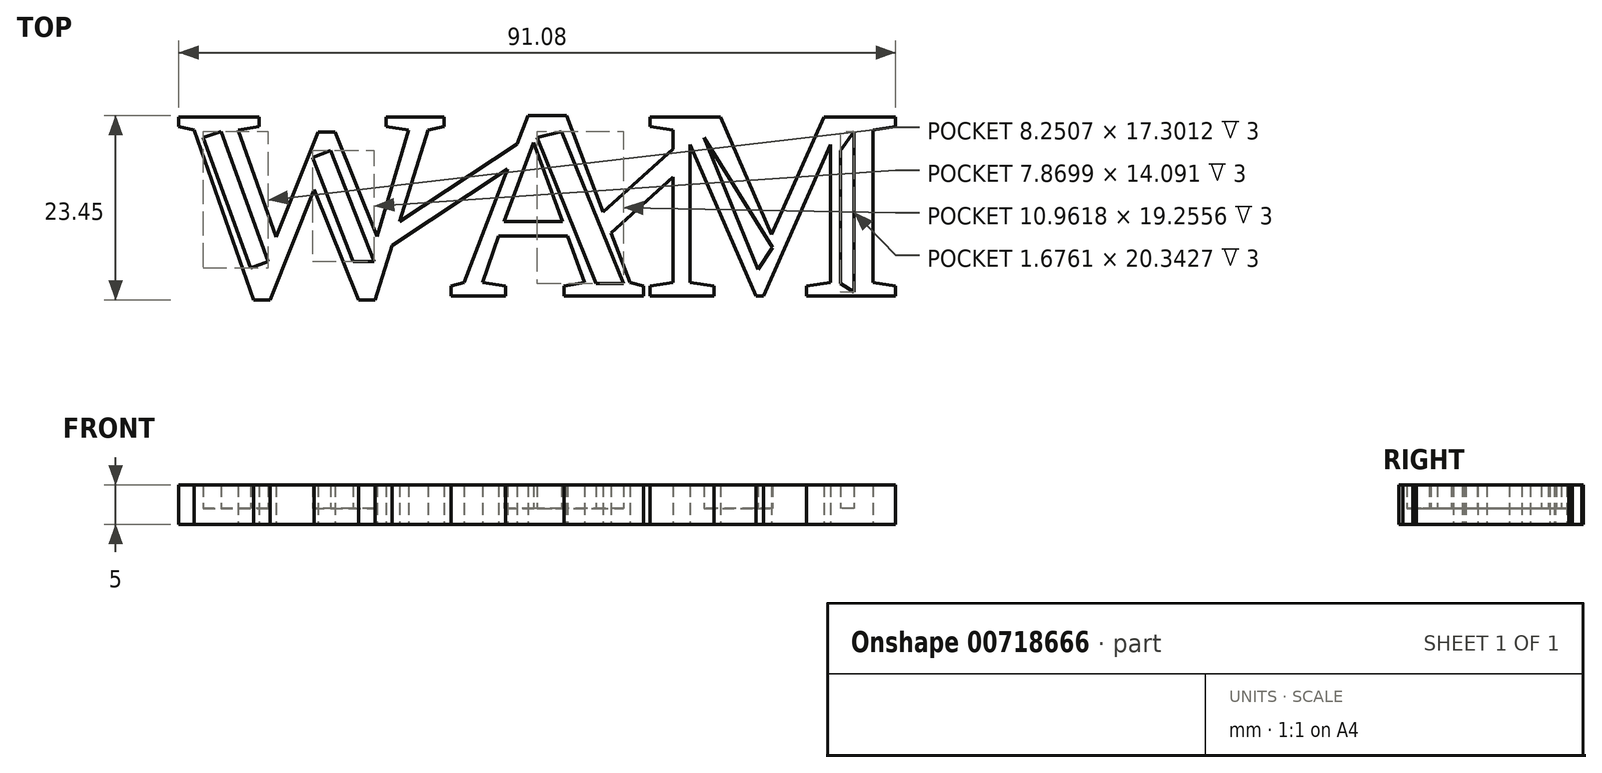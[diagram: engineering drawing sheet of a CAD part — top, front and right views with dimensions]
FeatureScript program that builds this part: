
annotation { "Feature Type Name" : "Feature", "Feature Type Description" : "" }
export const myFeature = defineFeature(function(context is Context, id is Id, definition is map)
    precondition{}
    {
        {
            var Q0;
            Q0=qCreatedBy(makeId("Top.planeOp"),FACE);
            var sketch = newSketch(context, id + "F0", { "sketchPlane" : qUnion([Q0])});
            skText(sketch, "E0", { "text": "WAM", "fontName": "Tinos-Bold.ttf"});
            skLineSegment(sketch, "E1", {"start": v(-3.4, 6.82) * mm, "end": v(-18.4, -3.1) * mm});
            skLineSegment(sketch, "E2", {"start": v(-4.59, 3.66) * mm, "end": v(-19.45, -6.25) * mm});
            skLineSegment(sketch, "E3", {"start": v(16.44, 2.6) * mm, "end": v(8.52, -4.52) * mm});
            skLineSegment(sketch, "E4", {"start": v(16.44, 6.16) * mm, "end": v(7.54, -1.84) * mm});
            skLineSegment(sketch, "E5", {"start": v(-41.01, 8.35) * mm, "end": v(-35.02, -8.14) * mm});
            skLineSegment(sketch, "E6", {"start": v(-35.02, -8.14) * mm, "end": v(-37.25, -8.95) * mm});
            skLineSegment(sketch, "E7", {"start": v(-37.25, -8.95) * mm, "end": v(-43.27, 7.6) * mm});
            skLineSegment(sketch, "E8", {"start": v(-43.27, 7.6) * mm, "end": v(-41.01, 8.35) * mm});
            skLineSegment(sketch, "E9", {"start": v(-27.07, 5.95) * mm, "end": v(-21.53, -8.14) * mm});
            skLineSegment(sketch, "E10", {"start": v(-21.53, -8.14) * mm, "end": v(-24.23, -8.14) * mm});
            skLineSegment(sketch, "E11", {"start": v(-24.23, -8.14) * mm, "end": v(-29.4, 5.05) * mm});
            skLineSegment(sketch, "E12", {"start": v(-29.4, 5.05) * mm, "end": v(-27.07, 5.95) * mm});
            skLineSegment(sketch, "E13", {"start": v(2.27, 8.35) * mm, "end": v(-0.83, 7.6) * mm});
            skLineSegment(sketch, "E14", {"start": v(-0.83, 7.6) * mm, "end": v(6.66, -10.9) * mm});
            skLineSegment(sketch, "E15", {"start": v(6.66, -10.9) * mm, "end": v(10.13, -10.9) * mm});
            skLineSegment(sketch, "E16", {"start": v(10.13, -10.9) * mm, "end": v(2.27, 8.35) * mm});
            skLineSegment(sketch, "E17", {"start": v(20.38, 7.6) * mm, "end": v(27.21, -9.15) * mm});
            skLineSegment(sketch, "E18", {"start": v(27.21, -9.15) * mm, "end": v(29.03, -6.34) * mm});
            skLineSegment(sketch, "E19", {"start": v(29.03, -6.34) * mm, "end": v(20.38, 7.6) * mm});
            skLineSegment(sketch, "E20", {"start": v(37.7, 5.95) * mm, "end": v(37.7, -10.9) * mm});
            skLineSegment(sketch, "E21", {"start": v(37.7, -10.9) * mm, "end": v(39.37, -12) * mm});
            skLineSegment(sketch, "E22", {"start": v(39.37, -12) * mm, "end": v(39.37, 8.35) * mm});
            skLineSegment(sketch, "E23", {"start": v(39.37, 8.35) * mm, "end": v(37.7, 5.95) * mm});
            const initialGuessF0  = {"E0": [-0.04687, -0.0125, 1, 0, 0.025]};
            skSetInitialGuess(sketch, initialGuessF0);
            skSolve(sketch);
        }
        {
            var Q0;
            {var subQ4=sQuery(id+"F0.wireOp",EDGE,"E0.sketch_text.stroke-0");Q0=makeQuery(id+"F0.imprint","IMPRINT",FACE,{"disambiguationData":[TD([[makeQuery(id+"F0.imprint","IMPRINT",EDGE,{"derivedFrom":subQ4}),-1.0]])]});}
            var Q1;
            {var subQ0=sQuery(id+"F0.wireOp",EDGE,"E1");var subQ1=sQuery(id+"F0.wireOp",EDGE,"E0.sketch_text.stroke-20");var subQ2=makeQuery(id+"F0.imprint","INTERSECT",VERTEX,{"derivedFrom":[subQ1,subQ0]});Q1=makeQuery(id+"F0.imprint","IMPRINT",FACE,{"disambiguationData":[TD([[makeQuery(id+"F0.imprint","IMPRINT",EDGE,{"disambiguationData":[TD([[subQ2,-1.0]])],"derivedFrom":subQ1}),1.0]])]});}
            var Q2;
            Q2=makeQuery(id+"F0.imprint","IMPRINT",FACE,{"disambiguationData":[TD([[makeQuery(id+"F0.imprint","IMPRINT",EDGE,{"derivedFrom":sQuery(id+"F0.wireOp",EDGE,"E0.sketch_text.stroke-21")}),-1.0]])]});
            var Q3;
            {var subQ0=sQuery(id+"F0.wireOp",EDGE,"E4");var subQ1=sQuery(id+"F0.wireOp",EDGE,"E0.sketch_text.stroke-27");var subQ2=makeQuery(id+"F0.imprint","INTERSECT",VERTEX,{"derivedFrom":[subQ1,subQ0]});Q3=makeQuery(id+"F0.imprint","IMPRINT",FACE,{"disambiguationData":[TD([[makeQuery(id+"F0.imprint","IMPRINT",EDGE,{"disambiguationData":[TD([[subQ2,-1.0]])],"derivedFrom":subQ1}),1.0]])]});}
            var Q4;
            Q4=makeQuery(id+"F0.imprint","IMPRINT",FACE,{"disambiguationData":[TD([[makeQuery(id+"F0.imprint","IMPRINT",EDGE,{"derivedFrom":sQuery(id+"F0.wireOp",EDGE,"E0.sketch_text.stroke-40")}),-1.0]])]});
            extrude(context, id + "F1", {"entities" : qUnion([Q0, Q1, Q2, Q3, Q4]), "depth" : 5 * mm, "offsetDistance" : 25 * mm});
        }
        {
            var Q0;
            Q0=makeQuery(id+"F0.imprint","IMPRINT",FACE,{"disambiguationData":[TD([[makeQuery(id+"F0.imprint","IMPRINT",EDGE,{"derivedFrom":sQuery(id+"F0.wireOp",EDGE,"E9")}),-1.0]])]});
            var Q1;
            Q1=makeQuery(id+"F0.imprint","IMPRINT",FACE,{"disambiguationData":[TD([[makeQuery(id+"F0.imprint","IMPRINT",EDGE,{"derivedFrom":sQuery(id+"F0.wireOp",EDGE,"E5")}),-1.0]])]});
            var Q2;
            Q2=makeQuery(id+"F0.imprint","IMPRINT",FACE,{"disambiguationData":[TD([[makeQuery(id+"F0.imprint","IMPRINT",EDGE,{"derivedFrom":sQuery(id+"F0.wireOp",EDGE,"E13")}),1.0]])]});
            var Q3;
            Q3=makeQuery(id+"F0.imprint","IMPRINT",FACE,{"disambiguationData":[TD([[makeQuery(id+"F0.imprint","IMPRINT",EDGE,{"derivedFrom":sQuery(id+"F0.wireOp",EDGE,"E0.sketch_text.stroke-37")}),1.0]])]});
            var Q4;
            Q4=makeQuery(id+"F0.imprint","IMPRINT",FACE,{"disambiguationData":[TD([[makeQuery(id+"F0.imprint","IMPRINT",EDGE,{"derivedFrom":sQuery(id+"F0.wireOp",EDGE,"E17")}),1.0]])]});
            var Q5;
            Q5=makeQuery(id+"F0.imprint","IMPRINT",FACE,{"disambiguationData":[TD([[makeQuery(id+"F0.imprint","IMPRINT",EDGE,{"derivedFrom":sQuery(id+"F0.wireOp",EDGE,"E20")}),1.0]])]});
            extrude(context, id + "F2", {"entities" : qUnion([Q0, Q1, Q2, Q3, Q4, Q5]), "operationType" : NewBodyOperationType.ADD, "depth" : 2 * mm, "offsetDistance" : 25 * mm});
        }
    });
